SOLIDWORKS PART (.sldprt)
format: sldprt  version: not decoded by parser v0  size: 201,728 bytes
history: native  units: mm
features: sketch x5, extrude x4, plane x3, material x1, cut_extrude x1, fillet x1 (+8 scaffold rows collapsed)
feature tree (23):
  scaffold x8  (default folders/planes/origin — collapsed)
  material  "Material <not specified>"
  plane  "Alzado"
  plane  "Planta"
  plane  "Vista lateral"
  sketch  "Croquis1"  dims[D1=71.0mm D2=7.0mm D3=3.5mm D4=35.5mm]
  extrude  "Extruir1"  Depth=5.5mm
  sketch  "Croquis2"  dims[D1=3.0mm D2=3.0mm D3=5.5mm]
  cut_extrude  "Cortar-Extruir1"  Depth=7.5mm
  sketch  "Croquis3"  dims[D1=7.5mm D2=4.0mm D3=4.0mm]
  extrude  "Extruir2"  [1 undecoded]
  sketch  "Croquis4"  dims[D1=16.5mm D2=1.0mm]
  extrude  "Cortar-Extruir2"  Depth=2.9mm
  fillet  "Redondeo1"  Radius=2mm
  sketch  "Croquis5"
  extrude  "Cortar-Extruir3"  Depth=2.9mm
decode coverage: 9 of 11 modeling features carry decoded parameters
note: 1 parameter value undecoded
note: suppression state not decoded; provenance and decode notes live in map.json
